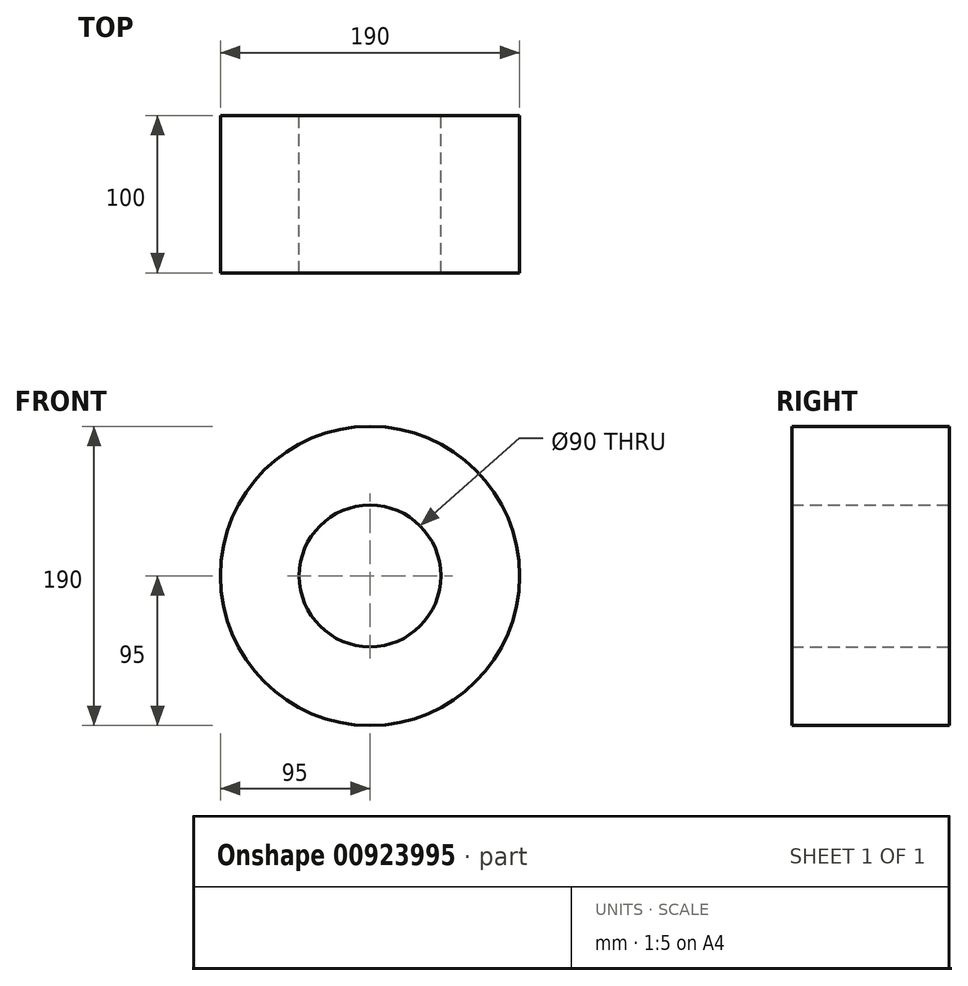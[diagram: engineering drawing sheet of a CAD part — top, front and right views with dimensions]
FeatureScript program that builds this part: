
annotation { "Feature Type Name" : "Feature", "Feature Type Description" : "" }
export const myFeature = defineFeature(function(context is Context, id is Id, definition is map)
    precondition{}
    {
        {
            var Q0;
            Q0=qCreatedBy(makeId("Front.planeOp"),FACE);
            var sketch = newSketch(context, id + "F0", { "sketchPlane" : qUnion([Q0])});
            skCircle(sketch, "E0", {"center": v(0, 0) * mm, "radius": 95 * mm});
            skCircle(sketch, "E1", {"center": v(0, 0) * mm, "radius": 45 * mm});
            skSolve(sketch);
        }
        {
            var Q0;
            Q0 = qSketchRegion(id + "F0", true);
            extrude(context, id + "F1", {"entities" : qUnion([Q0]), "depth" : 100 * mm, "offsetDistance" : 25 * mm});
        }
    });
